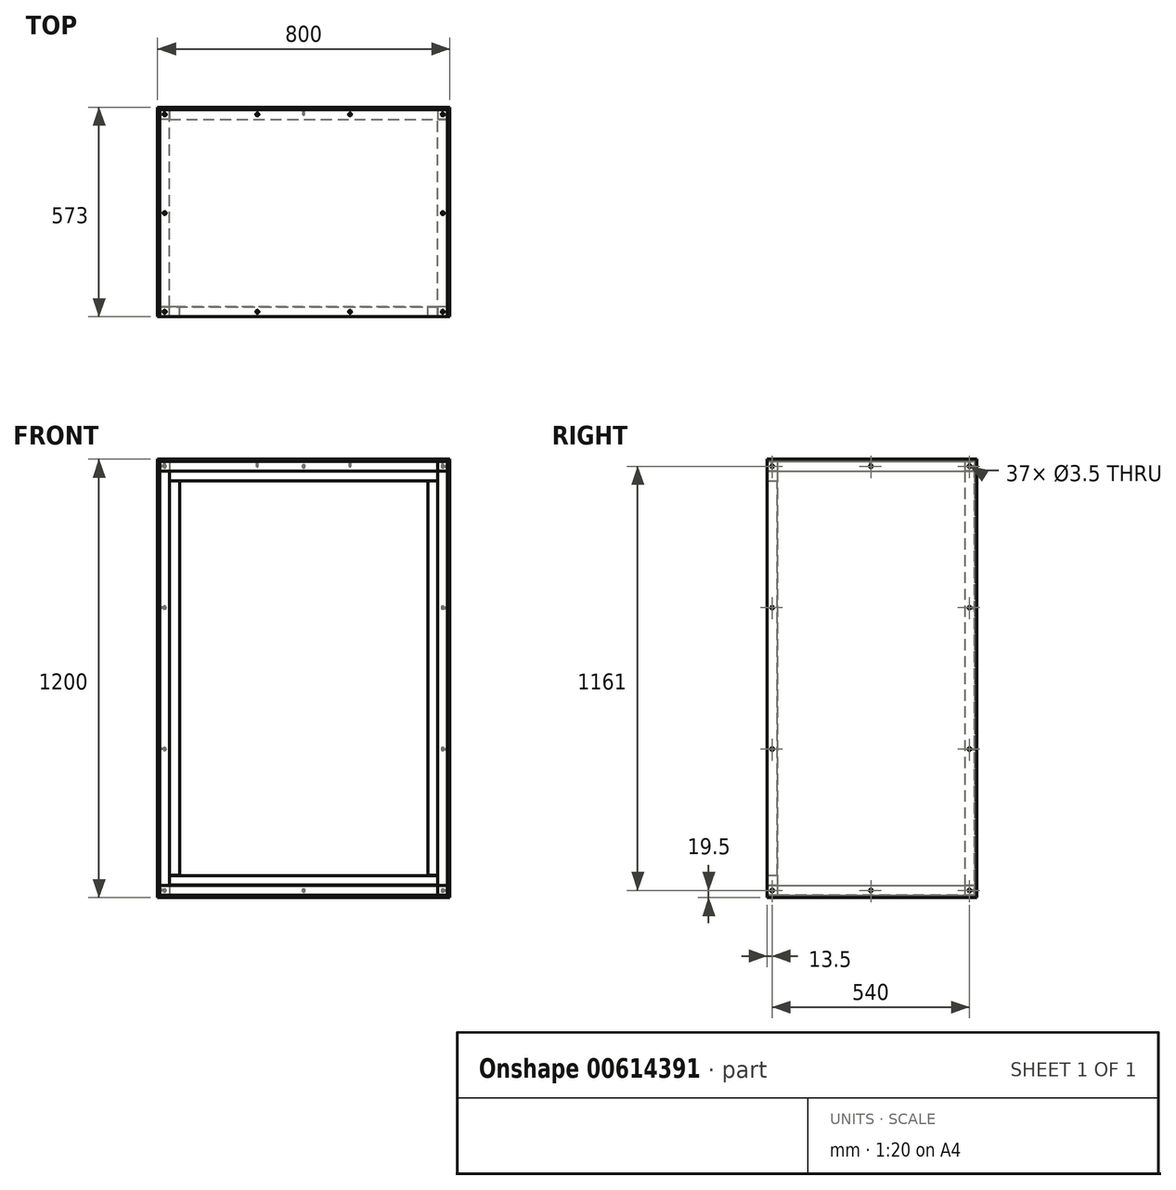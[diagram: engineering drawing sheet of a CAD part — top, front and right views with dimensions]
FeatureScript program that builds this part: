
annotation { "Feature Type Name" : "Feature", "Feature Type Description" : "" }
export const myFeature = defineFeature(function(context is Context, id is Id, definition is map)
    precondition{}
    {
        {
            assignVariable(context, id + "F0", {"name" : "width", "anyValue" : 800});
        }
        {
            assignVariable(context, id + "F1", {"name" : "height", "anyValue" : 1200});
        }
        {
            assignVariable(context, id + "F2", {"name" : "depth", "anyValue" : 600});
        }
        {
            assignVariable(context, id + "F3", {"name" : "thickness", "anyValue" : 6});
        }
        {
            assignVariable(context, id + "F4", {"name" : "reglar_size", "anyValue" : 27});
        }
        {
            assignVariable(context, id + "F5", {"name" : "screw_length", "anyValue" : 20});
        }
        {
            assignVariable(context, id + "F6", {"name" : "screw_hole_size", "anyValue" : 3.5});
        }
        {
            var Q0;
            Q0=qCreatedBy(makeId("Front.planeOp"),FACE);
            var sketch = newSketch(context, id + "F7", { "sketchPlane" : qUnion([Q0])});
            skLineSegment(sketch, "E0.bottom", {"start": v(507, -450) * mm, "end": v(-281, -450) * mm});
            skLineSegment(sketch, "E0.top", {"start": v(507, 750) * mm, "end": v(-281, 750) * mm});
            skLineSegment(sketch, "E0.left", {"start": v(507, -450) * mm, "end": v(507, 750) * mm});
            skLineSegment(sketch, "E0.right", {"start": v(-281, -450) * mm, "end": v(-281, 750) * mm});
            skLineSegment(sketch, "E1", {"start": v(-267.5, 730.5) * mm, "end": v(113, 730.5) * mm, "construction": true});
            skLineSegment(sketch, "E2", {"start": v(-267.5, -430.5) * mm, "end": v(-267.5, -43.5) * mm, "construction": true});
            skLineSegment(sketch, "E3", {"start": v(-267.5, -43.5) * mm, "end": v(-267.5, 343.5) * mm, "construction": true});
            skLineSegment(sketch, "E4", {"start": v(-267.5, 343.5) * mm, "end": v(-267.5, 730.5) * mm, "construction": true});
            skLineSegment(sketch, "E5", {"start": v(113, 730.5) * mm, "end": v(493.5, 730.5) * mm, "construction": true});
            skLineSegment(sketch, "E6", {"start": v(493.5, 730.5) * mm, "end": v(493.5, 343.5) * mm, "construction": true});
            skLineSegment(sketch, "E7", {"start": v(493.5, 343.5) * mm, "end": v(493.5, -43.5) * mm, "construction": true});
            skLineSegment(sketch, "E8", {"start": v(493.5, -43.5) * mm, "end": v(493.5, -430.5) * mm, "construction": true});
            skLineSegment(sketch, "E9", {"start": v(493.5, -430.5) * mm, "end": v(113, -430.5) * mm, "construction": true});
            skLineSegment(sketch, "E10", {"start": v(113, -430.5) * mm, "end": v(-267.5, -430.5) * mm, "construction": true});
            skSolve(sketch);
        }
        {
            var Q0;
            Q0=makeQuery(id+"F7.imprint","IMPRINT",FACE,{"disambiguationData":[TD([[makeQuery(id+"F7.imprint","IMPRINT",EDGE,{"derivedFrom":sQuery(id+"F7.wireOp",EDGE,"E0.bottom")}),-1.0]])]});
            extrude(context, id + "F8", {"entities" : qUnion([Q0]), "depth" : getVariable(context, 'thickness') * mm, "offsetDistance" : 25 * mm});
        }
        {
            var Q0;
            Q0=makeQuery(id+"F8.opExtrude","SWEPT_FACE",FACE,{"disambiguationData":[OSD([sQuery(id+"F7.wireOp",EDGE,"E0.left")])]});
            var sketch = newSketch(context, id + "F9", { "sketchPlane" : qUnion([Q0])});
            skLineSegment(sketch, "E11.bottom", {"start": v(-573, -450) * mm, "end": v(0, -450) * mm});
            skLineSegment(sketch, "E11.top", {"start": v(-573, 750) * mm, "end": v(0, 750) * mm});
            skLineSegment(sketch, "E11.left", {"start": v(-573, -450) * mm, "end": v(-573, 750) * mm});
            skLineSegment(sketch, "E11.right", {"start": v(0, -450) * mm, "end": v(0, 750) * mm});
            skLineSegment(sketch, "E12", {"start": v(-19.5, -430.5) * mm, "end": v(-19.5, -43.5) * mm, "construction": true});
            skLineSegment(sketch, "E13", {"start": v(-19.5, -43.5) * mm, "end": v(-19.5, 343.5) * mm, "construction": true});
            skLineSegment(sketch, "E14", {"start": v(-19.5, 343.5) * mm, "end": v(-19.5, 730.5) * mm, "construction": true});
            skLineSegment(sketch, "E15", {"start": v(-19.5, 730.5) * mm, "end": v(-289.5, 730.5) * mm, "construction": true});
            skLineSegment(sketch, "E16", {"start": v(-289.5, 730.5) * mm, "end": v(-559.5, 730.5) * mm, "construction": true});
            skLineSegment(sketch, "E17", {"start": v(-559.5, 730.5) * mm, "end": v(-559.5, 343.5) * mm, "construction": true});
            skLineSegment(sketch, "E18", {"start": v(-559.5, 343.5) * mm, "end": v(-559.5, -43.5) * mm, "construction": true});
            skLineSegment(sketch, "E19", {"start": v(-559.5, -43.5) * mm, "end": v(-559.5, -430.5) * mm, "construction": true});
            skLineSegment(sketch, "E20", {"start": v(-559.5, -430.5) * mm, "end": v(-289.5, -430.5) * mm, "construction": true});
            skLineSegment(sketch, "E21", {"start": v(-289.5, -430.5) * mm, "end": v(-19.5, -430.5) * mm, "construction": true});
            skSolve(sketch);
        }
        {
            var Q0;
            Q0 = qSketchRegion(id + "F9", true);
            extrude(context, id + "F10", {"entities" : qUnion([Q0]), "depth" : (getVariable(context, 'thickness')) * mm, "offsetDistance" : 25 * mm});
        }
        {
            var Q0;
            Q0=makeQuery(id+"F10.opExtrude","CAP_FACE",FACE,{"disambiguationData":[OSD([sQuery(id+"F9.wireOp",EDGE,"E11.bottom"),sQuery(id+"F9.wireOp",EDGE,"E11.top"),sQuery(id+"F9.wireOp",EDGE,"E11.left"),sQuery(id+"F9.wireOp",EDGE,"E11.right")])],"isStart":false});
            var sketch = newSketch(context, id + "F11", { "sketchPlane" : qUnion([Q0])});
            skLineSegment(sketch, "E22", {"start": v(-19.5, 730.5) * mm, "end": v(-19.5, 343.5) * mm, "construction": true});
            skLineSegment(sketch, "E23", {"start": v(-19.5, 343.5) * mm, "end": v(-19.5, -43.5) * mm, "construction": true});
            skLineSegment(sketch, "E24", {"start": v(-19.5, -43.5) * mm, "end": v(-19.5, -430.5) * mm, "construction": true});
            skLineSegment(sketch, "E25", {"start": v(-19.5, -430.5) * mm, "end": v(-289.5, -430.5) * mm, "construction": true});
            skLineSegment(sketch, "E26", {"start": v(-289.5, -430.5) * mm, "end": v(-559.5, -430.5) * mm, "construction": true});
            skLineSegment(sketch, "E27", {"start": v(-559.5, -430.5) * mm, "end": v(-559.5, -43.5) * mm, "construction": true});
            skLineSegment(sketch, "E28", {"start": v(-559.5, -43.5) * mm, "end": v(-559.5, 343.5) * mm, "construction": true});
            skLineSegment(sketch, "E29", {"start": v(-559.5, 343.5) * mm, "end": v(-559.5, 730.5) * mm, "construction": true});
            skLineSegment(sketch, "E30", {"start": v(-559.5, 730.5) * mm, "end": v(-289.5, 730.5) * mm, "construction": true});
            skLineSegment(sketch, "E31", {"start": v(-289.5, 730.5) * mm, "end": v(-19.5, 730.5) * mm, "construction": true});
            skSolve(sketch);
        }
        {
            var Q0;
            Q0=makeQuery(id+"F8.opExtrude","SWEPT_FACE",FACE,{"disambiguationData":[OSD([sQuery(id+"F7.wireOp",EDGE,"E0.bottom")])]});
            var sketch = newSketch(context, id + "F12", { "sketchPlane" : qUnion([Q0])});
            skLineSegment(sketch, "E32.bottom", {"start": v(507, 6) * mm, "end": v(480, 6) * mm});
            skLineSegment(sketch, "E32.top", {"start": v(507, 33) * mm, "end": v(480, 33) * mm});
            skLineSegment(sketch, "E32.left", {"start": v(507, 6) * mm, "end": v(507, 6) * mm});
            skLineSegment(sketch, "E32.right", {"start": v(480, 6) * mm, "end": v(480, 33) * mm});
            skLineSegment(sketch, "E33", {"start": v(507, 6) * mm, "end": v(507, 33) * mm});
            skSolve(sketch);
        }
        {
            var Q0;
            Q0=makeQuery(id+"F12.imprint","IMPRINT",FACE,{"disambiguationData":[TD([[makeQuery(id+"F12.imprint","IMPRINT",EDGE,{"derivedFrom":sQuery(id+"F12.wireOp",EDGE,"E32.bottom")}),-1.0]])]});
            extrude(context, id + "F13", {"entities" : qUnion([Q0]), "oppositeDirection" : true, "depth" : (getVariable(context, 'height') - getVariable(context, 'reglar_size') - getVariable(context, 'thickness')) * mm, "offsetDistance" : 25 * mm, "hasSecondDirection" : true, "secondDirectionOppositeDirection" : true, "secondDirectionDepth" : (getVariable(context, 'reglar_size') + getVariable(context, 'thickness')) * mm});
        }
        {
            var Q0;
            Q0=makeQuery(id+"F10.opExtrude","CAP_FACE",FACE,{"disambiguationData":[OSD([sQuery(id+"F9.wireOp",EDGE,"E11.bottom"),sQuery(id+"F9.wireOp",EDGE,"E11.top"),sQuery(id+"F9.wireOp",EDGE,"E11.left"),sQuery(id+"F9.wireOp",EDGE,"E11.right")])],"isStart":true});
            var sketch = newSketch(context, id + "F14", { "sketchPlane" : qUnion([Q0])});
            skLineSegment(sketch, "E34.bottom", {"start": v(6, -444) * mm, "end": v(33, -444) * mm});
            skLineSegment(sketch, "E34.top", {"start": v(6, -417) * mm, "end": v(33, -417) * mm});
            skLineSegment(sketch, "E34.left", {"start": v(33, -417) * mm, "end": v(33, -444) * mm});
            skLineSegment(sketch, "E34.right", {"start": v(6, -417) * mm, "end": v(6, -444) * mm});
            skLineSegment(sketch, "E35", {"start": v(19.5, 730.5) * mm, "end": v(19.5, -430.5) * mm, "construction": true});
            skSolve(sketch);
        }
        {
            var Q0;
            Q0 = qSketchRegion(id + "F14", true);
            extrude(context, id + "F15", {"entities" : qUnion([Q0]), "depth" : (getVariable(context, 'width') - getVariable(context, 'reglar_size') - getVariable(context, 'thickness') * 2) * mm, "offsetDistance" : 25 * mm});
        }
        {
            var Q0;
            Q0=makeQuery(id+"F13.opExtrude","SWEPT_FACE",FACE,{"disambiguationData":[OSD([sQuery(id+"F12.wireOp",EDGE,"E32.top")])]});
            var sketch = newSketch(context, id + "F16", { "sketchPlane" : qUnion([Q0])});
            skLineSegment(sketch, "E36.bottom", {"start": v(480, -444) * mm, "end": v(507, -444) * mm});
            skLineSegment(sketch, "E36.top", {"start": v(480, -417) * mm, "end": v(507, -417) * mm});
            skLineSegment(sketch, "E36.left", {"start": v(480, -417) * mm, "end": v(480, -444) * mm});
            skLineSegment(sketch, "E36.right", {"start": v(507, -417) * mm, "end": v(507, -444) * mm});
            skSolve(sketch);
        }
        {
            var Q0;
            Q0 = qSketchRegion(id + "F16", true);
            extrude(context, id + "F17", {"entities" : qUnion([Q0]), "depth" : (getVariable(context, 'depth') - (getVariable(context, 'reglar_size') * 2) - getVariable(context, 'thickness')) * mm, "offsetDistance" : 25 * mm});
        }
        {
            var Q0;
            Q0=makeQuery(id+"F13.opExtrude","SWEPT_BODY",BODY,{"disambiguationData":[OSD([sQuery(id+"F12.wireOp",EDGE,"E32.bottom"),sQuery(id+"F12.wireOp",EDGE,"E32.top"),sQuery(id+"F12.wireOp",EDGE,"E32.left"),sQuery(id+"F12.wireOp",EDGE,"E32.right")])]});
            var Q1;
            Q1=makeQuery(id+"F15.opExtrude","SWEPT_EDGE",EDGE,{"disambiguationData":[OSD([sQuery(id+"F14.wireOp",EDGE,"E34.bottom"),sQuery(id+"F14.wireOp",EDGE,"E34.right")])]});
            transform(context, id + "F18", {"entities" : qUnion([Q0]), "transformType" : TransformType.TRANSLATION_DISTANCE, "transformDirection" : qUnion([Q1]), "distance" : (getVariable(context, 'width') - getVariable(context, 'reglar_size') - getVariable(context, 'thickness') * 2) * mm, "oppositeDirection" : true, "makeCopy" : true});
        }
        {
            var Q0;
            Q0=makeQuery(id+"F13.opExtrude","SWEPT_BODY",BODY,{"disambiguationData":[OSD([sQuery(id+"F12.wireOp",EDGE,"E32.bottom"),sQuery(id+"F12.wireOp",EDGE,"E32.top"),sQuery(id+"F12.wireOp",EDGE,"E32.left"),sQuery(id+"F12.wireOp",EDGE,"E32.right")])]});
            var Q1;
            Q1=makeQuery(id+"F18.opPattern","COPY",BODY,{"derivedFrom":makeQuery(id+"F13.opExtrude","SWEPT_BODY",BODY,{"disambiguationData":[OSD([sQuery(id+"F12.wireOp",EDGE,"E32.bottom"),sQuery(id+"F12.wireOp",EDGE,"E32.top"),sQuery(id+"F12.wireOp",EDGE,"E32.left"),sQuery(id+"F12.wireOp",EDGE,"E32.right")])]}),"instanceName":"1"});
            var Q2;
            Q2=makeQuery(id+"F10.opExtrude","CAP_EDGE",EDGE,{"disambiguationData":[OSD([sQuery(id+"F9.wireOp",EDGE,"E11.bottom")])],"isStart":true});
            transform(context, id + "F19", {"entities" : qUnion([Q0, Q1]), "transformType" : TransformType.TRANSLATION_DISTANCE, "transformDirection" : qUnion([Q2]), "distance" : (getVariable(context, 'depth') - (getVariable(context, 'reglar_size') * 2) - getVariable(context, 'thickness')) * mm, "oppositeDirection" : true, "makeCopy" : true});
        }
        {
            var Q0;
            Q0=makeQuery(id+"F15.opExtrude","SWEPT_BODY",BODY,{"disambiguationData":[OSD([sQuery(id+"F14.wireOp",EDGE,"E34.bottom"),sQuery(id+"F14.wireOp",EDGE,"E34.top"),sQuery(id+"F14.wireOp",EDGE,"E34.left"),sQuery(id+"F14.wireOp",EDGE,"E34.right")])]});
            var Q1;
            Q1=makeQuery(id+"F13.opExtrude","SWEPT_EDGE",EDGE,{"disambiguationData":[OSD([sQuery(id+"F12.wireOp",EDGE,"E32.bottom"),sQuery(id+"F12.wireOp",EDGE,"E32.right")])]});
            transform(context, id + "F20", {"entities" : qUnion([Q0]), "transformType" : TransformType.TRANSLATION_DISTANCE, "transformDirection" : qUnion([Q1]), "distance" : (getVariable(context, 'height') - getVariable(context, 'reglar_size') - getVariable(context, 'thickness') * 2) * mm, "oppositeDirection" : true, "makeCopy" : true});
        }
        {
            var Q0;
            Q0=makeQuery(id+"F15.opExtrude","SWEPT_BODY",BODY,{"disambiguationData":[OSD([sQuery(id+"F14.wireOp",EDGE,"E34.bottom"),sQuery(id+"F14.wireOp",EDGE,"E34.top"),sQuery(id+"F14.wireOp",EDGE,"E34.left"),sQuery(id+"F14.wireOp",EDGE,"E34.right")])]});
            var Q1;
            Q1=makeQuery(id+"F20.opPattern","COPY",BODY,{"derivedFrom":makeQuery(id+"F15.opExtrude","SWEPT_BODY",BODY,{"disambiguationData":[OSD([sQuery(id+"F14.wireOp",EDGE,"E34.bottom"),sQuery(id+"F14.wireOp",EDGE,"E34.top"),sQuery(id+"F14.wireOp",EDGE,"E34.left"),sQuery(id+"F14.wireOp",EDGE,"E34.right")])]}),"instanceName":"1"});
            var Q2;
            Q2=makeQuery(id+"F17.opExtrude","SWEPT_EDGE",EDGE,{"disambiguationData":[OSD([sQuery(id+"F12.wireOp",EDGE,"E32.bottom"),sQuery(id+"F12.wireOp",EDGE,"E32.right"),sQuery(id+"F16.wireOp",EDGE,"E36.top"),sQuery(id+"F16.wireOp",EDGE,"E36.left")])]});
            transform(context, id + "F21", {"entities" : qUnion([Q0, Q1]), "transformType" : TransformType.TRANSLATION_3D, "dx" : (-getVariable(context, 'reglar_size')) * mm, "dy" : -(getVariable(context, 'depth') - (getVariable(context, 'reglar_size') * 2) - getVariable(context, 'thickness')) * mm, "dz" : 0 * mm, "makeCopy" : true});
        }
        {
            var Q0;
            Q0=makeQuery(id+"F17.opExtrude","SWEPT_BODY",BODY,{"disambiguationData":[OSD([sQuery(id+"F16.wireOp",EDGE,"E36.bottom"),sQuery(id+"F16.wireOp",EDGE,"E36.top"),sQuery(id+"F16.wireOp",EDGE,"E36.left"),sQuery(id+"F16.wireOp",EDGE,"E36.right")])]});
            var Q1;
            Q1=makeQuery(id+"F13.opExtrude","SWEPT_EDGE",EDGE,{"disambiguationData":[OSD([sQuery(id+"F12.wireOp",EDGE,"E32.bottom"),sQuery(id+"F12.wireOp",EDGE,"E32.right")])]});
            transform(context, id + "F22", {"entities" : qUnion([Q0]), "transformType" : TransformType.TRANSLATION_DISTANCE, "transformDirection" : qUnion([Q1]), "distance" : (getVariable(context, 'height') - getVariable(context, 'reglar_size') - getVariable(context, 'thickness') * 2) * mm, "oppositeDirection" : true, "makeCopy" : true});
        }
        {
            var Q0;
            Q0=makeQuery(id+"F17.opExtrude","SWEPT_BODY",BODY,{"disambiguationData":[OSD([sQuery(id+"F16.wireOp",EDGE,"E36.bottom"),sQuery(id+"F16.wireOp",EDGE,"E36.top"),sQuery(id+"F16.wireOp",EDGE,"E36.left"),sQuery(id+"F16.wireOp",EDGE,"E36.right")])]});
            var Q1;
            Q1=makeQuery(id+"F22.opPattern","COPY",BODY,{"derivedFrom":makeQuery(id+"F17.opExtrude","SWEPT_BODY",BODY,{"disambiguationData":[OSD([sQuery(id+"F16.wireOp",EDGE,"E36.bottom"),sQuery(id+"F16.wireOp",EDGE,"E36.top"),sQuery(id+"F16.wireOp",EDGE,"E36.left"),sQuery(id+"F16.wireOp",EDGE,"E36.right")])]}),"instanceName":"1"});
            var Q2;
            Q2=makeQuery(id+"F15.opExtrude","SWEPT_EDGE",EDGE,{"disambiguationData":[OSD([sQuery(id+"F12.wireOp",EDGE,"E32.bottom"),sQuery(id+"F12.wireOp",EDGE,"E32.right"),sQuery(id+"F14.wireOp",EDGE,"E34.top"),sQuery(id+"F14.wireOp",EDGE,"E34.right")])]});
            transform(context, id + "F23", {"entities" : qUnion([Q0, Q1]), "transformType" : TransformType.TRANSLATION_3D, "dx" : -(getVariable(context, 'width') - getVariable(context, 'reglar_size') - getVariable(context, 'thickness') * 2) * mm, "dy" : (getVariable(context, 'reglar_size')) * mm, "dz" : 0 * mm, "makeCopy" : true});
        }
        {
            var Q0;
            Q0=makeQuery(id+"F10.opExtrude","SWEPT_BODY",BODY,{"disambiguationData":[OSD([sQuery(id+"F9.wireOp",EDGE,"E11.bottom"),sQuery(id+"F9.wireOp",EDGE,"E11.top"),sQuery(id+"F9.wireOp",EDGE,"E11.left"),sQuery(id+"F9.wireOp",EDGE,"E11.right")])]});
            var Q1;
            Q1=makeQuery(id+"F22.opPattern","COPY",FACE,{"derivedFrom":makeQuery(id+"F17.opExtrude","SWEPT_FACE",FACE,{"disambiguationData":[OSD([sQuery(id+"F16.wireOp",EDGE,"E36.left")])]}),"instanceName":"1"});
            mirror(context, id + "F24", {"entities" : qUnion([Q0]), "mirrorPlane" : qUnion([Q1])});
        }
        {
            var Q0;
            Q0=makeQuery(id+"F24.opPattern","COPY",BODY,{"derivedFrom":makeQuery(id+"F10.opExtrude","SWEPT_BODY",BODY,{"disambiguationData":[OSD([sQuery(id+"F9.wireOp",EDGE,"E11.bottom"),sQuery(id+"F9.wireOp",EDGE,"E11.top"),sQuery(id+"F9.wireOp",EDGE,"E11.left"),sQuery(id+"F9.wireOp",EDGE,"E11.right")])]}),"instanceName":"1"});
            var Q1;
            Q1=makeQuery(id+"F15.opExtrude","SWEPT_EDGE",EDGE,{"disambiguationData":[OSD([sQuery(id+"F14.wireOp",EDGE,"E34.bottom"),sQuery(id+"F14.wireOp",EDGE,"E34.right")])]});
            transform(context, id + "F25", {"entities" : qUnion([Q0]), "transformType" : TransformType.TRANSLATION_3D, "dx" : -(getVariable(context, 'width') - getVariable(context, 'reglar_size') * 2 - getVariable(context, 'thickness') * 2) * mm, "dy" : 0 * mm, "dz" : 0 * mm, "makeCopy" : false});
        }
        {
            var Q0;
            Q0=makeQuery(id+"F24.opPattern","COPY",FACE,{"derivedFrom":makeQuery(id+"F10.opExtrude","CAP_FACE",FACE,{"disambiguationData":[OSD([sQuery(id+"F9.wireOp",EDGE,"E11.bottom"),sQuery(id+"F9.wireOp",EDGE,"E11.top"),sQuery(id+"F9.wireOp",EDGE,"E11.left"),sQuery(id+"F9.wireOp",EDGE,"E11.right")])],"isStart":false}),"instanceName":"1"});
            var sketch = newSketch(context, id + "F26", { "sketchPlane" : qUnion([Q0])});
            skLineSegment(sketch, "E37", {"start": v(559.5, 730.5) * mm, "end": v(559.5, 343.5) * mm, "construction": true});
            skLineSegment(sketch, "E38", {"start": v(559.5, 343.5) * mm, "end": v(559.5, -43.5) * mm, "construction": true});
            skLineSegment(sketch, "E39", {"start": v(559.5, -43.5) * mm, "end": v(559.5, -430.5) * mm, "construction": true});
            skLineSegment(sketch, "E40", {"start": v(559.5, -430.5) * mm, "end": v(289.5, -430.5) * mm, "construction": true});
            skLineSegment(sketch, "E41", {"start": v(289.5, -430.5) * mm, "end": v(19.5, -430.5) * mm, "construction": true});
            skLineSegment(sketch, "E42", {"start": v(19.5, -430.5) * mm, "end": v(19.5, -43.5) * mm, "construction": true});
            skLineSegment(sketch, "E43", {"start": v(19.5, -43.5) * mm, "end": v(19.5, 343.5) * mm, "construction": true});
            skLineSegment(sketch, "E44", {"start": v(19.5, 343.5) * mm, "end": v(19.5, 730.5) * mm, "construction": true});
            skLineSegment(sketch, "E45", {"start": v(19.5, 730.5) * mm, "end": v(289.5, 730.5) * mm, "construction": true});
            skLineSegment(sketch, "E46", {"start": v(289.5, 730.5) * mm, "end": v(559.5, 730.5) * mm, "construction": true});
            skSolve(sketch);
        }
        {
            var Q0;
            Q0=makeQuery(id+"F23.opPattern","COPY",FACE,{"derivedFrom":makeQuery(id+"F22.opPattern","COPY",FACE,{"derivedFrom":makeQuery(id+"F17.opExtrude","SWEPT_FACE",FACE,{"disambiguationData":[OSD([sQuery(id+"F16.wireOp",EDGE,"E36.top")])]}),"instanceName":"1"}),"instanceName":"1"});
            var sketch = newSketch(context, id + "F27", { "sketchPlane" : qUnion([Q0])});
            skLineSegment(sketch, "E47.bottom", {"start": v(-281, -6) * mm, "end": v(507, -6) * mm});
            skLineSegment(sketch, "E47.top", {"start": v(-281, -573) * mm, "end": v(507, -573) * mm});
            skLineSegment(sketch, "E47.left", {"start": v(-281, -6) * mm, "end": v(-281, -573) * mm});
            skLineSegment(sketch, "E47.right", {"start": v(507, -6) * mm, "end": v(507, -573) * mm});
            skSolve(sketch);
        }
        {
            var Q0;
            Q0 = qSketchRegion(id + "F27", true);
            extrude(context, id + "F28", {"entities" : qUnion([Q0]), "depth" : (getVariable(context, 'thickness')) * mm, "offsetDistance" : 25 * mm});
        }
        {
            var Q0;
            Q0=makeQuery(id+"F28.opExtrude","CAP_FACE",FACE,{"disambiguationData":[OSD([sQuery(id+"F27.wireOp",EDGE,"E47.bottom"),sQuery(id+"F27.wireOp",EDGE,"E47.top"),sQuery(id+"F27.wireOp",EDGE,"E47.left"),sQuery(id+"F27.wireOp",EDGE,"E47.right")])],"isStart":false});
            var sketch = newSketch(context, id + "F29", { "sketchPlane" : qUnion([Q0])});
            skLineSegment(sketch, "E48", {"start": v(493.5, -19.5) * mm, "end": v(493.5, -289.5) * mm, "construction": true});
            skLineSegment(sketch, "E49", {"start": v(493.5, -289.5) * mm, "end": v(493.5, -559.5) * mm, "construction": true});
            skLineSegment(sketch, "E50", {"start": v(493.5, -559.5) * mm, "end": v(239.83, -559.5) * mm, "construction": true});
            skLineSegment(sketch, "E51", {"start": v(239.83, -559.5) * mm, "end": v(-13.83, -559.5) * mm, "construction": true});
            skLineSegment(sketch, "E52", {"start": v(-13.83, -559.5) * mm, "end": v(-267.5, -559.5) * mm, "construction": true});
            skLineSegment(sketch, "E53", {"start": v(-267.5, -559.5) * mm, "end": v(-267.5, -289.5) * mm, "construction": true});
            skLineSegment(sketch, "E54", {"start": v(-267.5, -289.5) * mm, "end": v(-267.5, -19.5) * mm, "construction": true});
            skLineSegment(sketch, "E55", {"start": v(-267.5, -19.5) * mm, "end": v(-13.83, -19.5) * mm, "construction": true});
            skLineSegment(sketch, "E56", {"start": v(-13.83, -19.5) * mm, "end": v(239.83, -19.5) * mm, "construction": true});
            skLineSegment(sketch, "E57", {"start": v(239.83, -19.5) * mm, "end": v(493.5, -19.5) * mm, "construction": true});
            skSolve(sketch);
        }
        {
            var Q0;
            Q0=sQuery(id+"F7.wireOp",VERTEX,"E9.end");
            var Q1;
            Q1=sQuery(id+"F7.wireOp",VERTEX,"E3.start");
            var Q2;
            Q2=sQuery(id+"F7.wireOp",VERTEX,"E8.start");
            var Q3;
            Q3=sQuery(id+"F7.wireOp",VERTEX,"E7.start");
            var Q4;
            Q4=sQuery(id+"F7.wireOp",VERTEX,"E1.end");
            var Q5;
            Q5=sQuery(id+"F7.wireOp",VERTEX,"E4.start");
            var Q6;
            Q6=sQuery(id+"F7.wireOp",VERTEX,"E6.start");
            var Q7;
            Q7=sQuery(id+"F7.wireOp",VERTEX,"E1.start");
            var Q8;
            Q8=sQuery(id+"F7.wireOp",VERTEX,"E2.start");
            var Q9;
            Q9=sQuery(id+"F7.wireOp",VERTEX,"E9.start");
            var Q10;
            Q10=makeQuery(id+"F13.opExtrude","SWEPT_BODY",BODY,{"disambiguationData":[OSD([sQuery(id+"F12.wireOp",EDGE,"E32.bottom"),sQuery(id+"F12.wireOp",EDGE,"E32.top"),sQuery(id+"F12.wireOp",EDGE,"E32.left"),sQuery(id+"F12.wireOp",EDGE,"E32.right")])]});
            var Q11;
            Q11=makeQuery(id+"F18.opPattern","COPY",BODY,{"derivedFrom":makeQuery(id+"F13.opExtrude","SWEPT_BODY",BODY,{"disambiguationData":[OSD([sQuery(id+"F12.wireOp",EDGE,"E32.bottom"),sQuery(id+"F12.wireOp",EDGE,"E32.top"),sQuery(id+"F12.wireOp",EDGE,"E32.left"),sQuery(id+"F12.wireOp",EDGE,"E32.right")])]}),"instanceName":"1"});
            var Q12;
            Q12=makeQuery(id+"F15.opExtrude","SWEPT_BODY",BODY,{"disambiguationData":[OSD([sQuery(id+"F14.wireOp",EDGE,"E34.bottom"),sQuery(id+"F14.wireOp",EDGE,"E34.top"),sQuery(id+"F14.wireOp",EDGE,"E34.left"),sQuery(id+"F14.wireOp",EDGE,"E34.right")])]});
            var Q13;
            Q13=makeQuery(id+"F20.opPattern","COPY",BODY,{"derivedFrom":makeQuery(id+"F15.opExtrude","SWEPT_BODY",BODY,{"disambiguationData":[OSD([sQuery(id+"F14.wireOp",EDGE,"E34.bottom"),sQuery(id+"F14.wireOp",EDGE,"E34.top"),sQuery(id+"F14.wireOp",EDGE,"E34.left"),sQuery(id+"F14.wireOp",EDGE,"E34.right")])]}),"instanceName":"1"});
            var Q14;
            Q14=makeQuery(id+"F8.opExtrude","SWEPT_BODY",BODY,{"disambiguationData":[OSD([sQuery(id+"F7.wireOp",EDGE,"E0.bottom"),sQuery(id+"F7.wireOp",EDGE,"E0.top"),sQuery(id+"F7.wireOp",EDGE,"E0.left"),sQuery(id+"F7.wireOp",EDGE,"E0.right")])]});
            hole(context, id + "F30", {"style" : HoleStyle.C_SINK, "endStyle" : HoleEndStyle.BLIND, "oppositeDirection" : true, "holeDiameter" : (getVariable(context, 'screw_hole_size')) * mm, "cSinkDiameter" : 8 * mm, "cSinkAngle" : 90 * degree, "majorDiameter" : 5 * mm, "holeDepth" : getVariable(context, 'screw_length') * mm, "isTappedThrough" : true, "tappedDepth" : 12 * mm, "tapClearance" : 3, "locations" : qUnion([Q0, Q1, Q2, Q3, Q4, Q5, Q6, Q7, Q8, Q9]), "scope" : qUnion([Q10, Q11, Q12, Q13, Q14])});
        }
        {
            var Q0;
            Q0=sQuery(id+"F11.wireOp",VERTEX,"E30.end");
            var Q1;
            Q1=sQuery(id+"F11.wireOp",VERTEX,"E23.start");
            var Q2;
            Q2=sQuery(id+"F11.wireOp",VERTEX,"E24.start");
            var Q3;
            Q3=sQuery(id+"F11.wireOp",VERTEX,"E26.start");
            var Q4;
            Q4=sQuery(id+"F11.wireOp",VERTEX,"E28.start");
            var Q5;
            Q5=sQuery(id+"F11.wireOp",VERTEX,"E28.end");
            var Q6;
            Q6=sQuery(id+"F11.wireOp",VERTEX,"E29.end");
            var Q7;
            Q7=sQuery(id+"F11.wireOp",VERTEX,"E31.end");
            var Q8;
            Q8=sQuery(id+"F11.wireOp",VERTEX,"E25.start");
            var Q9;
            Q9=sQuery(id+"F11.wireOp",VERTEX,"E27.start");
            var Q10;
            Q10=sQuery(id+"F26.wireOp",VERTEX,"E44.end");
            var Q11;
            Q11=sQuery(id+"F26.wireOp",VERTEX,"E45.end");
            var Q12;
            Q12=sQuery(id+"F26.wireOp",VERTEX,"E37.start");
            var Q13;
            Q13=sQuery(id+"F26.wireOp",VERTEX,"E44.start");
            var Q14;
            Q14=sQuery(id+"F26.wireOp",VERTEX,"E38.start");
            var Q15;
            Q15=sQuery(id+"F26.wireOp",VERTEX,"E39.start");
            var Q16;
            Q16=sQuery(id+"F26.wireOp",VERTEX,"E43.start");
            var Q17;
            Q17=sQuery(id+"F26.wireOp",VERTEX,"E42.start");
            var Q18;
            Q18=sQuery(id+"F26.wireOp",VERTEX,"E41.start");
            var Q19;
            Q19=sQuery(id+"F26.wireOp",VERTEX,"E40.start");
            var Q20;
            Q20=sQuery(id+"F29.wireOp",VERTEX,"E55.start");
            var Q21;
            Q21=sQuery(id+"F29.wireOp",VERTEX,"E55.end");
            var Q22;
            Q22=sQuery(id+"F29.wireOp",VERTEX,"E54.start");
            var Q23;
            Q23=sQuery(id+"F29.wireOp",VERTEX,"E53.start");
            var Q24;
            Q24=sQuery(id+"F29.wireOp",VERTEX,"E52.start");
            var Q25;
            Q25=sQuery(id+"F29.wireOp",VERTEX,"E51.start");
            var Q26;
            Q26=sQuery(id+"F29.wireOp",VERTEX,"E50.start");
            var Q27;
            Q27=sQuery(id+"F29.wireOp",VERTEX,"E49.start");
            var Q28;
            Q28=sQuery(id+"F29.wireOp",VERTEX,"E57.end");
            var Q29;
            Q29=sQuery(id+"F29.wireOp",VERTEX,"E57.start");
            var Q30;
            Q30=makeQuery(id+"F10.opExtrude","SWEPT_BODY",BODY,{"disambiguationData":[OSD([sQuery(id+"F9.wireOp",EDGE,"E11.bottom"),sQuery(id+"F9.wireOp",EDGE,"E11.top"),sQuery(id+"F9.wireOp",EDGE,"E11.left"),sQuery(id+"F9.wireOp",EDGE,"E11.right")])]});
            var Q31;
            Q31=makeQuery(id+"F17.opExtrude","SWEPT_BODY",BODY,{"disambiguationData":[OSD([sQuery(id+"F16.wireOp",EDGE,"E36.bottom"),sQuery(id+"F16.wireOp",EDGE,"E36.top"),sQuery(id+"F16.wireOp",EDGE,"E36.left"),sQuery(id+"F16.wireOp",EDGE,"E36.right")])]});
            var Q32;
            Q32=makeQuery(id+"F19.opPattern","COPY",BODY,{"derivedFrom":makeQuery(id+"F13.opExtrude","SWEPT_BODY",BODY,{"disambiguationData":[OSD([sQuery(id+"F12.wireOp",EDGE,"E32.bottom"),sQuery(id+"F12.wireOp",EDGE,"E32.top"),sQuery(id+"F12.wireOp",EDGE,"E32.left"),sQuery(id+"F12.wireOp",EDGE,"E32.right")])]}),"instanceName":"1"});
            var Q33;
            Q33=makeQuery(id+"F13.opExtrude","SWEPT_BODY",BODY,{"disambiguationData":[OSD([sQuery(id+"F12.wireOp",EDGE,"E32.bottom"),sQuery(id+"F12.wireOp",EDGE,"E32.top"),sQuery(id+"F12.wireOp",EDGE,"E32.left"),sQuery(id+"F12.wireOp",EDGE,"E32.right")])]});
            var Q34;
            Q34=makeQuery(id+"F22.opPattern","COPY",BODY,{"derivedFrom":makeQuery(id+"F17.opExtrude","SWEPT_BODY",BODY,{"disambiguationData":[OSD([sQuery(id+"F16.wireOp",EDGE,"E36.bottom"),sQuery(id+"F16.wireOp",EDGE,"E36.top"),sQuery(id+"F16.wireOp",EDGE,"E36.left"),sQuery(id+"F16.wireOp",EDGE,"E36.right")])]}),"instanceName":"1"});
            var Q35;
            Q35=makeQuery(id+"F24.opPattern","COPY",BODY,{"derivedFrom":makeQuery(id+"F10.opExtrude","SWEPT_BODY",BODY,{"disambiguationData":[OSD([sQuery(id+"F9.wireOp",EDGE,"E11.bottom"),sQuery(id+"F9.wireOp",EDGE,"E11.top"),sQuery(id+"F9.wireOp",EDGE,"E11.left"),sQuery(id+"F9.wireOp",EDGE,"E11.right")])]}),"instanceName":"1"});
            var Q36;
            Q36=makeQuery(id+"F18.opPattern","COPY",BODY,{"derivedFrom":makeQuery(id+"F13.opExtrude","SWEPT_BODY",BODY,{"disambiguationData":[OSD([sQuery(id+"F12.wireOp",EDGE,"E32.bottom"),sQuery(id+"F12.wireOp",EDGE,"E32.top"),sQuery(id+"F12.wireOp",EDGE,"E32.left"),sQuery(id+"F12.wireOp",EDGE,"E32.right")])]}),"instanceName":"1"});
            var Q37;
            Q37=makeQuery(id+"F23.opPattern","COPY",BODY,{"derivedFrom":makeQuery(id+"F17.opExtrude","SWEPT_BODY",BODY,{"disambiguationData":[OSD([sQuery(id+"F16.wireOp",EDGE,"E36.bottom"),sQuery(id+"F16.wireOp",EDGE,"E36.top"),sQuery(id+"F16.wireOp",EDGE,"E36.left"),sQuery(id+"F16.wireOp",EDGE,"E36.right")])]}),"instanceName":"1"});
            var Q38;
            Q38=makeQuery(id+"F19.opPattern","COPY",BODY,{"derivedFrom":makeQuery(id+"F18.opPattern","COPY",BODY,{"derivedFrom":makeQuery(id+"F13.opExtrude","SWEPT_BODY",BODY,{"disambiguationData":[OSD([sQuery(id+"F12.wireOp",EDGE,"E32.bottom"),sQuery(id+"F12.wireOp",EDGE,"E32.top"),sQuery(id+"F12.wireOp",EDGE,"E32.left"),sQuery(id+"F12.wireOp",EDGE,"E32.right")])]}),"instanceName":"1"}),"instanceName":"1"});
            var Q39;
            Q39=makeQuery(id+"F23.opPattern","COPY",BODY,{"derivedFrom":makeQuery(id+"F22.opPattern","COPY",BODY,{"derivedFrom":makeQuery(id+"F17.opExtrude","SWEPT_BODY",BODY,{"disambiguationData":[OSD([sQuery(id+"F16.wireOp",EDGE,"E36.bottom"),sQuery(id+"F16.wireOp",EDGE,"E36.top"),sQuery(id+"F16.wireOp",EDGE,"E36.left"),sQuery(id+"F16.wireOp",EDGE,"E36.right")])]}),"instanceName":"1"}),"instanceName":"1"});
            var Q40;
            Q40=makeQuery(id+"F28.opExtrude","SWEPT_BODY",BODY,{"disambiguationData":[OSD([sQuery(id+"F27.wireOp",EDGE,"E47.bottom"),sQuery(id+"F27.wireOp",EDGE,"E47.top"),sQuery(id+"F27.wireOp",EDGE,"E47.left"),sQuery(id+"F27.wireOp",EDGE,"E47.right")])]});
            var Q41;
            Q41=makeQuery(id+"F21.opPattern","COPY",BODY,{"derivedFrom":makeQuery(id+"F20.opPattern","COPY",BODY,{"derivedFrom":makeQuery(id+"F15.opExtrude","SWEPT_BODY",BODY,{"disambiguationData":[OSD([sQuery(id+"F14.wireOp",EDGE,"E34.bottom"),sQuery(id+"F14.wireOp",EDGE,"E34.top"),sQuery(id+"F14.wireOp",EDGE,"E34.left"),sQuery(id+"F14.wireOp",EDGE,"E34.right")])]}),"instanceName":"1"}),"instanceName":"1"});
            hole(context, id + "F31", {"style" : HoleStyle.C_SINK, "endStyle" : HoleEndStyle.BLIND, "holeDiameter" : (getVariable(context, 'screw_hole_size')) * mm, "cSinkDiameter" : 8 * mm, "cSinkAngle" : 90 * degree, "majorDiameter" : 5 * mm, "holeDepth" : getVariable(context, 'screw_length') * mm, "isTappedThrough" : true, "tappedDepth" : 12 * mm, "tapClearance" : 3, "locations" : qUnion([Q0, Q1, Q2, Q3, Q4, Q5, Q6, Q7, Q8, Q9, Q10, Q11, Q12, Q13, Q14, Q15, Q16, Q17, Q18, Q19, Q20, Q21, Q22, Q23, Q24, Q25, Q26, Q27, Q28, Q29]), "scope" : qUnion([Q30, Q31, Q32, Q33, Q34, Q35, Q36, Q37, Q38, Q39, Q40, Q41])});
        }
        {
            var Q0;
            Q0=makeQuery(id+"F28.opExtrude","SWEPT_BODY",BODY,{"disambiguationData":[OSD([sQuery(id+"F27.wireOp",EDGE,"E47.bottom"),sQuery(id+"F27.wireOp",EDGE,"E47.top"),sQuery(id+"F27.wireOp",EDGE,"E47.left"),sQuery(id+"F27.wireOp",EDGE,"E47.right")])]});
            var Q1;
            Q1=makeQuery(id+"F28.opExtrude","CAP_FACE",FACE,{"disambiguationData":[OSD([sQuery(id+"F27.wireOp",EDGE,"E47.bottom"),sQuery(id+"F27.wireOp",EDGE,"E47.top"),sQuery(id+"F27.wireOp",EDGE,"E47.left"),sQuery(id+"F27.wireOp",EDGE,"E47.right")])],"isStart":false});
            mirror(context, id + "F32", {"entities" : qUnion([Q0]), "mirrorPlane" : qUnion([Q1])});
        }
        {
            var Q0;
            Q0=makeQuery(id+"F32.opPattern","COPY",BODY,{"derivedFrom":makeQuery(id+"F28.opExtrude","SWEPT_BODY",BODY,{"disambiguationData":[OSD([sQuery(id+"F27.wireOp",EDGE,"E47.bottom"),sQuery(id+"F27.wireOp",EDGE,"E47.top"),sQuery(id+"F27.wireOp",EDGE,"E47.left"),sQuery(id+"F27.wireOp",EDGE,"E47.right")])]}),"instanceName":"1"});
            var Q1;
            Q1=makeQuery(id+"F19.opPattern","COPY",EDGE,{"derivedFrom":makeQuery(id+"F13.opExtrude","SWEPT_EDGE",EDGE,{"disambiguationData":[OSD([sQuery(id+"F12.wireOp",EDGE,"E32.top"),sQuery(id+"F12.wireOp",EDGE,"E32.right")])]}),"instanceName":"1"});
            var Q2;
            Q2=makeQuery(id+"F19.opPattern","COPY",EDGE,{"derivedFrom":makeQuery(id+"F13.opExtrude","SWEPT_EDGE",EDGE,{"disambiguationData":[OSD([sQuery(id+"F12.wireOp",EDGE,"E32.top"),sQuery(id+"F12.wireOp",EDGE,"E32.right")])]}),"instanceName":"1"});
            transform(context, id + "F33", {"entities" : qUnion([Q0]), "transformType" : TransformType.TRANSLATION_DISTANCE, "transformDirection" : qUnion([Q2]), "distance" : (getVariable(context, 'height')) * mm, "makeCopy" : false});
        }
        {
            var Q0;
            Q0=makeQuery(id+"F19.opPattern","COPY",FACE,{"derivedFrom":makeQuery(id+"F18.opPattern","COPY",FACE,{"derivedFrom":makeQuery(id+"F13.opExtrude","SWEPT_FACE",FACE,{"disambiguationData":[OSD([sQuery(id+"F12.wireOp",EDGE,"E33")])]}),"instanceName":"1"}),"instanceName":"1"});
            var sketch = newSketch(context, id + "F34", { "sketchPlane" : qUnion([Q0])});
            skLineSegment(sketch, "E58.bottom", {"start": v(-573, 717) * mm, "end": v(-546, 717) * mm});
            skLineSegment(sketch, "E58.top", {"start": v(-573, 691.02) * mm, "end": v(-546, 691.02) * mm});
            skLineSegment(sketch, "E58.left", {"start": v(-573, 717) * mm, "end": v(-573, 691.02) * mm});
            skLineSegment(sketch, "E58.right", {"start": v(-546, 717) * mm, "end": v(-546, 691.02) * mm});
            skSolve(sketch);
        }
        {
            var Q0;
            Q0 = qSketchRegion(id + "F34", true);
            extrude(context, id + "F35", {"entities" : qUnion([Q0]), "depth" : (getVariable(context, 'width') - getVariable(context, 'reglar_size') * 2 - getVariable(context, 'thickness') * 2) * mm, "offsetDistance" : 25 * mm});
        }
        {
            var Q0;
            Q0=makeQuery(id+"F35.opExtrude","SWEPT_FACE",FACE,{"disambiguationData":[OSD([sQuery(id+"F34.wireOp",EDGE,"E58.top")])]});
            var sketch = newSketch(context, id + "F36", { "sketchPlane" : qUnion([Q0])});
            skLineSegment(sketch, "E59.bottom", {"start": v(-254, 573) * mm, "end": v(-227, 573) * mm});
            skLineSegment(sketch, "E59.top", {"start": v(-254, 546) * mm, "end": v(-227, 546) * mm});
            skLineSegment(sketch, "E59.left", {"start": v(-254, 573) * mm, "end": v(-254, 546) * mm});
            skLineSegment(sketch, "E59.right", {"start": v(-227, 573) * mm, "end": v(-227, 546) * mm});
            skSolve(sketch);
        }
        {
            var Q0;
            Q0 = qSketchRegion(id + "F36", true);
            extrude(context, id + "F37", {"entities" : qUnion([Q0]), "depth" : (getVariable(context, 'height') - getVariable(context, 'reglar_size') * 4 - getVariable(context, 'thickness') * 2) * mm, "offsetDistance" : 25 * mm});
        }
        {
            var Q0;
            Q0=makeQuery(id+"F35.opExtrude","SWEPT_BODY",BODY,{"disambiguationData":[OSD([sQuery(id+"F34.wireOp",EDGE,"E58.bottom"),sQuery(id+"F34.wireOp",EDGE,"E58.top"),sQuery(id+"F34.wireOp",EDGE,"E58.left"),sQuery(id+"F34.wireOp",EDGE,"E58.right")])]});
            var Q1;
            Q1=makeQuery(id+"F19.opPattern","COPY",EDGE,{"derivedFrom":makeQuery(id+"F13.opExtrude","SWEPT_EDGE",EDGE,{"disambiguationData":[OSD([sQuery(id+"F12.wireOp",EDGE,"E32.top"),sQuery(id+"F12.wireOp",EDGE,"E32.right")])]}),"instanceName":"1"});
            transform(context, id + "F38", {"entities" : qUnion([Q0]), "transformType" : TransformType.TRANSLATION_DISTANCE, "transformDirection" : qUnion([Q1]), "distance" : (getVariable(context, 'height') - getVariable(context, 'reglar_size') * 3 - getVariable(context, 'thickness') * 2) * mm, "makeCopy" : true});
        }
        {
            var Q0;
            Q0=makeQuery(id+"F37.opExtrude","SWEPT_BODY",BODY,{"disambiguationData":[OSD([sQuery(id+"F36.wireOp",EDGE,"E59.bottom"),sQuery(id+"F36.wireOp",EDGE,"E59.top"),sQuery(id+"F36.wireOp",EDGE,"E59.left"),sQuery(id+"F36.wireOp",EDGE,"E59.right")])]});
            var Q1;
            Q1=makeQuery(id+"F35.opExtrude","SWEPT_EDGE",EDGE,{"disambiguationData":[OSD([sQuery(id+"F12.wireOp",EDGE,"E32.top"),sQuery(id+"F12.wireOp",EDGE,"E33"),sQuery(id+"F34.wireOp",EDGE,"E58.top"),sQuery(id+"F34.wireOp",EDGE,"E58.left")])]});
            var Q2;
            Q2=makeQuery(id+"F21.opPattern","COPY",EDGE,{"derivedFrom":makeQuery(id+"F20.opPattern","COPY",EDGE,{"derivedFrom":makeQuery(id+"F15.opExtrude","SWEPT_EDGE",EDGE,{"disambiguationData":[OSD([sQuery(id+"F14.wireOp",EDGE,"E34.bottom"),sQuery(id+"F14.wireOp",EDGE,"E34.left")])]}),"instanceName":"1"}),"instanceName":"1"});
            transform(context, id + "F39", {"entities" : qUnion([Q0]), "transformType" : TransformType.TRANSLATION_DISTANCE, "transformDirection" : qUnion([Q2]), "distance" : (getVariable(context, 'width') - getVariable(context, 'reglar_size') * 3 - getVariable(context, 'thickness') * 2) * mm, "makeCopy" : true});
        }
    });
